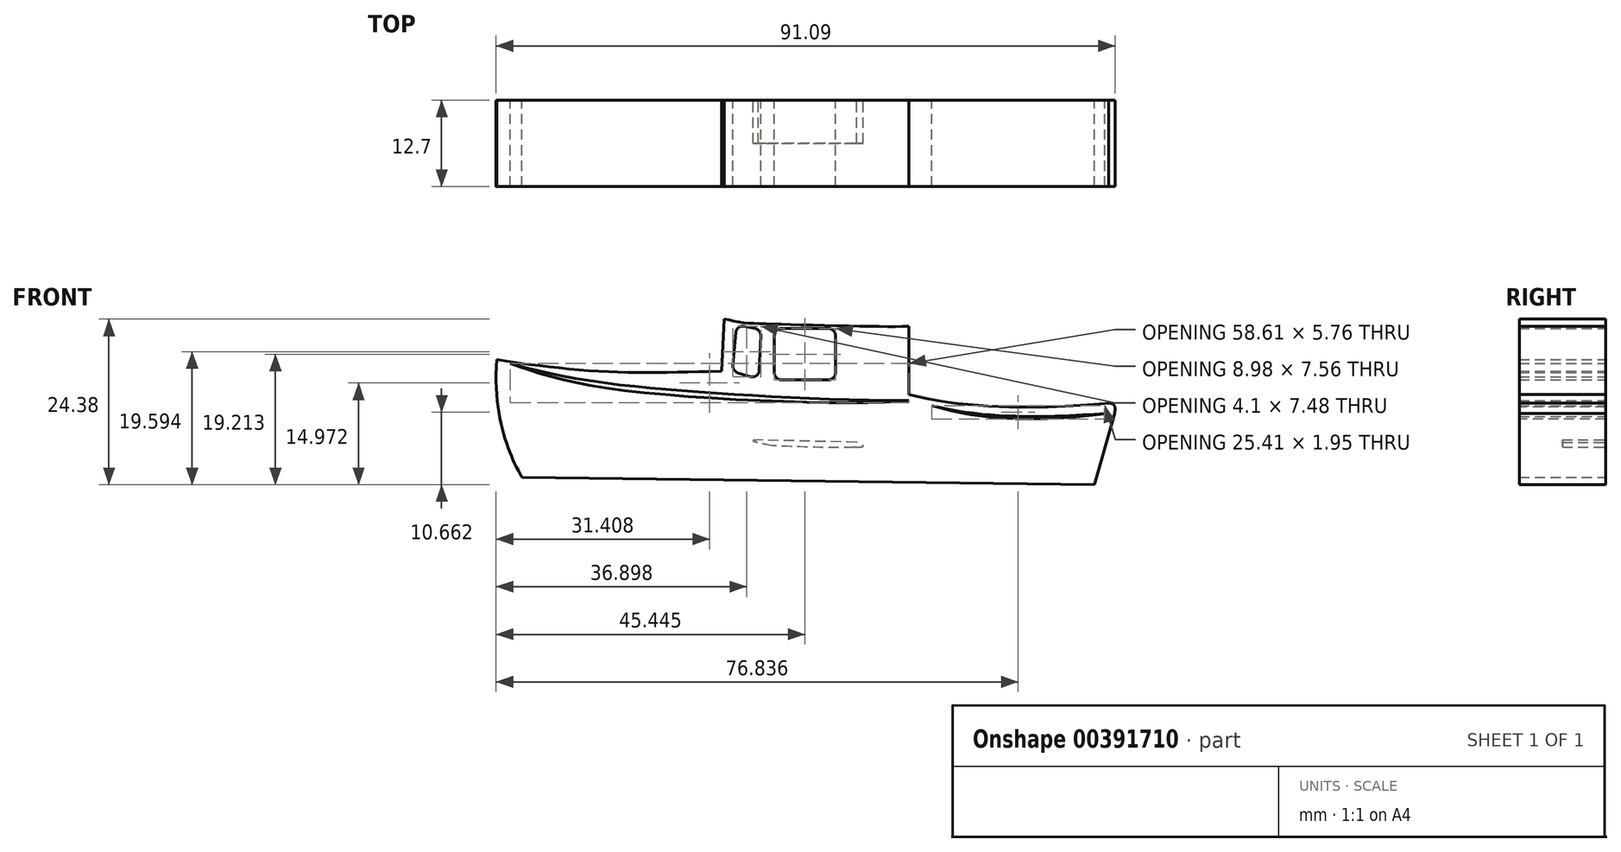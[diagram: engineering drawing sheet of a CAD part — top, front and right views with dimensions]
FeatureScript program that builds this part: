
annotation { "Feature Type Name" : "Feature", "Feature Type Description" : "" }
export const myFeature = defineFeature(function(context is Context, id is Id, definition is map)
    precondition{}
    {
        {
            var Q0;
            Q0=qCreatedBy(makeId("Front.planeOp"),FACE);
            var sketch = newSketch(context, id + "F0", { "sketchPlane" : qUnion([Q0])});
            skFitSpline(sketch, "E0", {"points": [v(-22.43, 15.47) * mm, v(-9.62, 13.25) * mm, v(8.37, 12.44) * mm], "startDerivative": vector(32.76, -9.72) * mm, "endDerivative": vector(35.18, -0.06) * mm});
            skFitSpline(sketch, "E1", {"points": [v(8.37, 12.44) * mm, v(23.03, 11.52) * mm], "startDerivative": vector(15.59, -5.38) * mm, "endDerivative": vector(6.87, 0.19) * mm});
            skFitSpline(sketch, "E2", {"points": [v(-22.43, 15.47) * mm, v(-21.75, 9.41) * mm, v(-20.57, 6.82) * mm], "startDerivative": vector(-0.94, -12.8) * mm, "endDerivative": vector(3.25, -5.62) * mm});
            skLineSegment(sketch, "E3", {"start": v(-20.57, 6.82) * mm, "end": v(21.55, 6.26) * mm});
            skLineSegment(sketch, "E4", {"start": v(23.03, 11.52) * mm, "end": v(21.55, 6.26) * mm});
            skFitSpline(sketch, "E5", {"points": [v(23.03, 11.52) * mm, v(23.03, 12.03) * mm, v(22.6, 12.27) * mm], "startDerivative": vector(0.26, 1.95) * mm, "endDerivative": vector(-1.75, -0.07) * mm});
            skLineSegment(sketch, "E6", {"start": v(8.1, 18.75) * mm, "end": v(-6.39, 19.1) * mm});
            skFitSpline(sketch, "E7", {"points": [v(-6.39, 19.1) * mm, v(-6.39, 18.74) * mm, v(-2.93, 18.24) * mm, v(8.7, 18.07) * mm, v(8.1, 18.75) * mm], "startDerivative": vector(-47.71, -1.19) * mm, "endDerivative": vector(-27.16, 12.33) * mm});
            skLineSegment(sketch, "E8", {"start": v(-5.68, 18.58) * mm, "end": v(-5.87, 14.61) * mm});
            skFitSpline(sketch, "E9", {"points": [v(-5.87, 14.61) * mm, v(-14.98, 14.61) * mm, v(-22.43, 15.47) * mm], "startDerivative": vector(-19.99, -0.5) * mm, "endDerivative": vector(-12.78, 2.15) * mm});
            skLineSegment(sketch, "E10.bottom", {"start": v(-1.5, 17.76) * mm, "end": v(1.98, 17.76) * mm});
            skLineSegment(sketch, "E10.top", {"start": v(-1.5, 13.98) * mm, "end": v(1.98, 13.98) * mm});
            skLineSegment(sketch, "E10.left", {"start": v(-2, 17.25) * mm, "end": v(-2, 14.48) * mm});
            skLineSegment(sketch, "E10.right", {"start": v(2.49, 17.25) * mm, "end": v(2.49, 14.48) * mm});
            skPoint(sketch, "E11.visualSharp", {"position": v(-2, 17.76) * mm});
            skArc(sketch, "E11.filletArc", {"start": v(-1.5, 17.76) * mm, "mid": v(-1.85, 17.6) * mm, "end": v(-2, 17.25) * mm});
            skPoint(sketch, "E12.visualSharp", {"position": v(2.49, 17.76) * mm});
            skArc(sketch, "E12.filletArc", {"start": v(2.49, 17.25) * mm, "mid": v(2.34, 17.6) * mm, "end": v(1.98, 17.76) * mm});
            skPoint(sketch, "E13.visualSharp", {"position": v(-2, 13.98) * mm});
            skArc(sketch, "E13.filletArc", {"start": v(-2, 14.48) * mm, "mid": v(-1.85, 14.13) * mm, "end": v(-1.5, 13.98) * mm});
            skPoint(sketch, "E14.visualSharp", {"position": v(2.49, 13.98) * mm});
            skArc(sketch, "E14.filletArc", {"start": v(1.98, 13.98) * mm, "mid": v(2.34, 14.13) * mm, "end": v(2.49, 14.48) * mm});
            skLineSegment(sketch, "E15", {"start": v(-4.7, 14.5) * mm, "end": v(-3.77, 14.2) * mm});
            skLineSegment(sketch, "E16", {"start": v(-3.12, 14.67) * mm, "end": v(-3, 17.23) * mm});
            skLineSegment(sketch, "E17", {"start": v(-3.41, 17.75) * mm, "end": v(-4.23, 17.92) * mm});
            skLineSegment(sketch, "E18", {"start": v(-4.84, 17.46) * mm, "end": v(-5.05, 15.02) * mm});
            skPoint(sketch, "E19.visualSharp", {"position": v(-4.8, 18.03) * mm});
            skArc(sketch, "E19.filletArc", {"start": v(-4.23, 17.92) * mm, "mid": v(-4.64, 17.83) * mm, "end": v(-4.84, 17.46) * mm});
            skPoint(sketch, "E20.visualSharp", {"position": v(-3.14, 14.02) * mm});
            skArc(sketch, "E20.filletArc", {"start": v(-3.77, 14.2) * mm, "mid": v(-3.33, 14.28) * mm, "end": v(-3.12, 14.67) * mm});
            skPoint(sketch, "E21.visualSharp", {"position": v(-2.99, 17.66) * mm});
            skArc(sketch, "E21.filletArc", {"start": v(-3, 17.23) * mm, "mid": v(-3.11, 17.56) * mm, "end": v(-3.41, 17.75) * mm});
            skPoint(sketch, "E22.visualSharp", {"position": v(-5.1, 14.61) * mm});
            skArc(sketch, "E22.filletArc", {"start": v(-5.05, 15.02) * mm, "mid": v(-4.97, 14.7) * mm, "end": v(-4.7, 14.5) * mm});
            skLineSegment(sketch, "E23", {"start": v(7.88, 18.04) * mm, "end": v(7.88, 12.91) * mm});
            skFitSpline(sketch, "E24", {"points": [v(-6.39, 19.1) * mm, v(-6.39, 18.74) * mm, v(-2.93, 18.24) * mm, v(8.7, 18.07) * mm, v(8.1, 18.75) * mm], "startDerivative": vector(-47.71, -1.19) * mm, "endDerivative": vector(-27.16, 12.33) * mm});
            skFitSpline(sketch, "E25", {"points": [v(7.88, 12.91) * mm, v(22.6, 12.27) * mm], "startDerivative": vector(15.53, -4.28) * mm, "endDerivative": vector(6.37, 0.65) * mm});
            skFitSpline(sketch, "E26", {"points": [v(-22.43, 15.47) * mm, v(-9.62, 13.25) * mm, v(8.37, 12.44) * mm], "startDerivative": vector(32.76, -9.72) * mm, "endDerivative": vector(35.18, -0.06) * mm});
            skFitSpline(sketch, "E27", {"points": [v(-21.43, 15.19) * mm, v(-13.14, 13.2) * mm, v(7.88, 12.45) * mm], "startDerivative": vector(15.27, -5.6) * mm, "endDerivative": vector(15.47, 1.77) * mm});
            skFitSpline(sketch, "E28", {"points": [v(8.37, 12.44) * mm, v(23.03, 11.52) * mm], "startDerivative": vector(15.59, -5.38) * mm, "endDerivative": vector(6.87, 0.19) * mm});
            skFitSpline(sketch, "E29", {"points": [v(8.37, 12.44) * mm, v(14.19, 11.2) * mm, v(22.3, 11.48) * mm], "startDerivative": vector(12.92, -4.07) * mm, "endDerivative": vector(14.9, 2.08) * mm});
            skLineSegment(sketch, "E30", {"start": v(7.88, 12.91) * mm, "end": v(7.88, 12.45) * mm});
            skFitSpline(sketch, "E31.0", {"points": [v(-6.39, 19.23) * mm, v(-6.51, 19.22) * mm, v(-6.73, 19.22) * mm, v(-6.93, 19.2) * mm, v(-7.04, 19.18) * mm, v(-7.12, 19.17) * mm, v(-7.17, 19.15) * mm, v(-7.2, 19.13) * mm, v(-7.23, 19.12) * mm, v(-7.27, 19.08) * mm, v(-7.3, 19.03) * mm, v(-7.3, 18.96) * mm, v(-7.27, 18.91) * mm, v(-7.24, 18.88) * mm, v(-7.21, 18.86) * mm, v(-7.17, 18.83) * mm, v(-7.12, 18.81) * mm, v(-7.05, 18.78) * mm, v(-6.94, 18.75) * mm, v(-6.79, 18.7) * mm, v(-6.62, 18.66) * mm, v(-6.45, 18.63) * mm, v(-6.24, 18.58) * mm, v(-6, 18.52) * mm, v(-5.73, 18.46) * mm, v(-5.5, 18.4) * mm, v(-5.2, 18.34) * mm, v(-4.9, 18.28) * mm, v(-4.56, 18.22) * mm, v(-4.26, 18.18) * mm, v(-3.95, 18.16) * mm, v(-3.61, 18.14) * mm, v(-3.21, 18.12) * mm, v(-2.73, 18.1) * mm, v(-2.14, 18.08) * mm, v(-1.24, 18.05) * mm, v(0.06, 18.01) * mm, v(1.78, 17.97) * mm, v(3.56, 17.93) * mm, v(4.99, 17.9) * mm, v(6.05, 17.9) * mm, v(6.78, 17.9) * mm, v(7.45, 17.9) * mm, v(7.93, 17.91) * mm, v(8.27, 17.92) * mm, v(8.5, 17.93) * mm, v(8.7, 17.95) * mm, v(8.84, 17.96) * mm, v(8.94, 17.97) * mm, v(9, 17.98) * mm, v(9.07, 18) * mm, v(9.12, 18.03) * mm, v(9.18, 18.07) * mm, v(9.2, 18.14) * mm, v(9.21, 18.21) * mm, v(9.18, 18.28) * mm, v(9.14, 18.34) * mm, v(9.08, 18.38) * mm, v(8.99, 18.45) * mm, v(8.82, 18.55) * mm, v(8.54, 18.69) * mm, v(8.3, 18.8) * mm, v(8.15, 18.87) * mm]});
            skLineSegment(sketch, "E32", {"start": v(-5.25, 18.35) * mm, "end": v(-5.22, 18.48) * mm});
            skLineSegment(sketch, "E33", {"start": v(7.53, 18.03) * mm, "end": v(7.53, 17.9) * mm});
            skLineSegment(sketch, "E34", {"start": v(-20.57, 6.82) * mm, "end": v(8.37, 12.44) * mm});
            skLineSegment(sketch, "E35", {"start": v(-20.57, 6.82) * mm, "end": v(22.16, 5.88) * mm});
            skLineSegment(sketch, "E36", {"start": v(22.16, 5.88) * mm, "end": v(23.03, 11.52) * mm});
            skSolve(sketch);
        }
        {
            var Q0;
            Q0=makeQuery(id+"F0.imprint","IMPRINT",FACE,{"disambiguationData":[TD([[makeQuery(id+"F0.imprint","IMPRINT",EDGE,{"derivedFrom":sQuery(id+"F0.wireOp",EDGE,"E0")}),1.0]])]});
            var Q1;
            Q1=makeQuery(id+"F0.imprint","IMPRINT",FACE,{"disambiguationData":[TD([[makeQuery(id+"F0.imprint","IMPRINT",EDGE,{"derivedFrom":sQuery(id+"F0.wireOp",EDGE,"E6")}),1.0]])]});
            var Q2;
            Q2=makeQuery(id+"F0.imprint","IMPRINT",FACE,{"disambiguationData":[TD([[makeQuery(id+"F0.imprint","IMPRINT",EDGE,{"derivedFrom":sQuery(id+"F0.wireOp",EDGE,"E5")}),1.0]])]});
            extrude(context, id + "F1", {"entities" : qUnion([Q0, Q1, Q2]), "depth" : 6.35 * mm});
        }
        {
            var Q0;
            Q0=makeQuery(id+"F0.imprint","IMPRINT",FACE,{"disambiguationData":[TD([[makeQuery(id+"F0.imprint","IMPRINT",EDGE,{"derivedFrom":sQuery(id+"F0.wireOp",EDGE,"E0")}),-1.0]])]});
            var Q1;
            Q1=makeQuery(id+"F0.imprint","IMPRINT",FACE,{"disambiguationData":[TD([[makeQuery(id+"F0.imprint","IMPRINT",EDGE,{"derivedFrom":sQuery(id+"F0.wireOp",EDGE,"E3")}),1.0]])]});
            extrude(context, id + "F2", {"entities" : qUnion([Q0, Q1]), "operationType" : NewBodyOperationType.ADD, "depth" : 6.35 * mm});
        }
        {
            var Q0;
            Q0=makeQuery(id+"F1.opExtrude","SWEPT_BODY",BODY,{"disambiguationData":[OSD([sQuery(id+"F0.wireOp",EDGE,"E0"),sQuery(id+"F0.wireOp",EDGE,"E1"),sQuery(id+"F0.wireOp",EDGE,"E5"),sQuery(id+"F0.wireOp",EDGE,"E6"),sQuery(id+"F0.wireOp",EDGE,"E7"),sQuery(id+"F0.wireOp",EDGE,"E8"),sQuery(id+"F0.wireOp",EDGE,"E9"),sQuery(id+"F0.wireOp",EDGE,"E10.bottom"),sQuery(id+"F0.wireOp",EDGE,"E10.top"),sQuery(id+"F0.wireOp",EDGE,"E10.left"),sQuery(id+"F0.wireOp",EDGE,"E10.right"),sQuery(id+"F0.wireOp",EDGE,"E11.filletArc"),sQuery(id+"F0.wireOp",EDGE,"E12.filletArc"),sQuery(id+"F0.wireOp",EDGE,"E13.filletArc"),sQuery(id+"F0.wireOp",EDGE,"E14.filletArc"),sQuery(id+"F0.wireOp",EDGE,"E15"),sQuery(id+"F0.wireOp",EDGE,"E16"),sQuery(id+"F0.wireOp",EDGE,"E17"),sQuery(id+"F0.wireOp",EDGE,"E18"),sQuery(id+"F0.wireOp",EDGE,"E19.filletArc"),sQuery(id+"F0.wireOp",EDGE,"E20.filletArc"),sQuery(id+"F0.wireOp",EDGE,"E21.filletArc"),sQuery(id+"F0.wireOp",EDGE,"E22.filletArc"),sQuery(id+"F0.wireOp",EDGE,"E23"),sQuery(id+"F0.wireOp",EDGE,"E24"),sQuery(id+"F0.wireOp",EDGE,"E25"),sQuery(id+"F0.wireOp",EDGE,"E26"),sQuery(id+"F0.wireOp",EDGE,"E0"),sQuery(id+"F0.wireOp",EDGE,"E28"),sQuery(id+"F0.wireOp",EDGE,"E29"),sQuery(id+"F0.wireOp",EDGE,"E7"),sQuery(id+"F0.wireOp",EDGE,"E31.0"),sQuery(id+"F0.wireOp",EDGE,"E32"),sQuery(id+"F0.wireOp",EDGE,"E33")])]});
            var Q1;
            Q1=qCreatedBy(makeId("Origin.pointOp"),VERTEX);
            transform(context, id + "F3", {"entities" : qUnion([Q0]), "transformType" : TransformType.SCALE_UNIFORMLY, "scale" : 2, "scalePoint" : qUnion([Q1]), "makeCopy" : false});
        }
    });
